# Revit family: sign_110-1330
name_source: partatom
category: Leuchten
revit_build: Autodesk Revit 2016 (Build: 20190508_0715(x64)
units: mm (PartAtom-declared; Revit-internal decimal feet)

## family parameters
Basisbauteil = Fläche
Beim Laden mit Abzugskörper schneiden = Nein
Bemaßung runder Anschluss = Durchmesser verwenden
Gemeinsam genutzt = Nein
Lichtquelle = Nein
Raumberechnungspunkt = Nein
Teiletyp = Normal

## types (1)
- 110-1330-D01-H30 (1 x LED, 1064.91 lm, 7.9 W, 3000K)
    Beschreibung = SIGN
    CIE Flux Codes = 48 79 95 100 58
    Color Rendering = 1B/80…89
    Color Temperature = 3000K
    Height = 0 mm  [stored 0 ft]
    Hersteller = Prolicht
    Lamp Light Flux = 1064.91 lm
    Lamp Power = 7.9 W
    Lamp count = 1
    Lampe = 1 x LED
    Length = 140 mm  [stored 0.459318 ft]
    Luminous efficacy = 79 lm/W
    ModVariant = Nein
    Modell = 110-1330
    Mounting Place = Ceiling
    Mounting Type = Recessed
    Number of Poles = 1
    OnlyDefault = Ja
    Power Factor = 1
    Product Name = SIGN
    Product group = Trimless recessed lights
    ProductGroupID = 411
    Protection Class = Protection class
    Protection Degree = Degree of protection
    RLX_Detail_Level = 1
    RlxData = <blob elided: 81181 chars, md5=231f692f>
    Scheinlast = 8 VA
    Socket = socket
    Standby Power = 0 W
    System Light Flux = 621 lm
    System Power = 8 W
    Typenbild = 110-1330.jpg
    Typenkommentare = DIFFUSER Opal (01),LED COLOUR DIR 3000 K (30)
    URL = http://relux.com
    VarID = 110-1330-d01-h30
    Voltage = 0 V
    Vorgabe-Ansicht = 1800 mm
    Weight = 0.00 kg
    Width = 0 mm  [stored 0 ft]

note: [stored X ft] marks values corroborated as IEEE doubles in the binary element streams (Revit-internal decimal feet)

## geometry (parser evidence)
native form markers: Blend x4, Sweep x14
no freeform markers — native parametric forms only
